# Revit family: rba-bim-rba2731-506
name_source: partatom
category: Plumbing Fixtures
revit_build: Autodesk Revit 2018 (Build: 20170223_1515(x64)
units: mm (PartAtom-declared; Revit-internal decimal feet)

## family parameters
Always vertical = No
Cut with Voids When Loaded = No
Part Type = Normal
Room Calculation Point = No
Round Connector Dimension = Use Diameter
Shared = No
Work Plane-Based = No

## types (1)
- RBA2731-506
    BCD - Bottle Counter Display = No
    CWFU = 1.5
    Cold Water Connection Diameter = 9.525 mm  [stored 0.03125 ft]
    Cold Water Connection Radius = 4.763 mm
    Description = H2O to Go!® Bottler Filler, Surface Mounted, Push Button
    Housing Material = Stainless Steel-Murdock-Satin
    Inner Panel Material = Steel-Murdock-Galvannealed
    Manufacturer = RBA Group
    Materials and Finishes = Stainless Steel-Murdock-Satin
    Model = RBA2731-506
    Modified Issue = 20210927.01
    Pushbutton Visibility = Yes
    Sensor Visibility = No
    URL = www.rba.com.au
    Waste Connection Radius = 19.05 mm  [stored 0.0625 ft]

note: [stored X ft] marks values corroborated as IEEE doubles in the binary element streams (Revit-internal decimal feet)

## geometry (parser evidence)
native form markers: Blend x6, Sweep x2
no freeform markers — native parametric forms only
